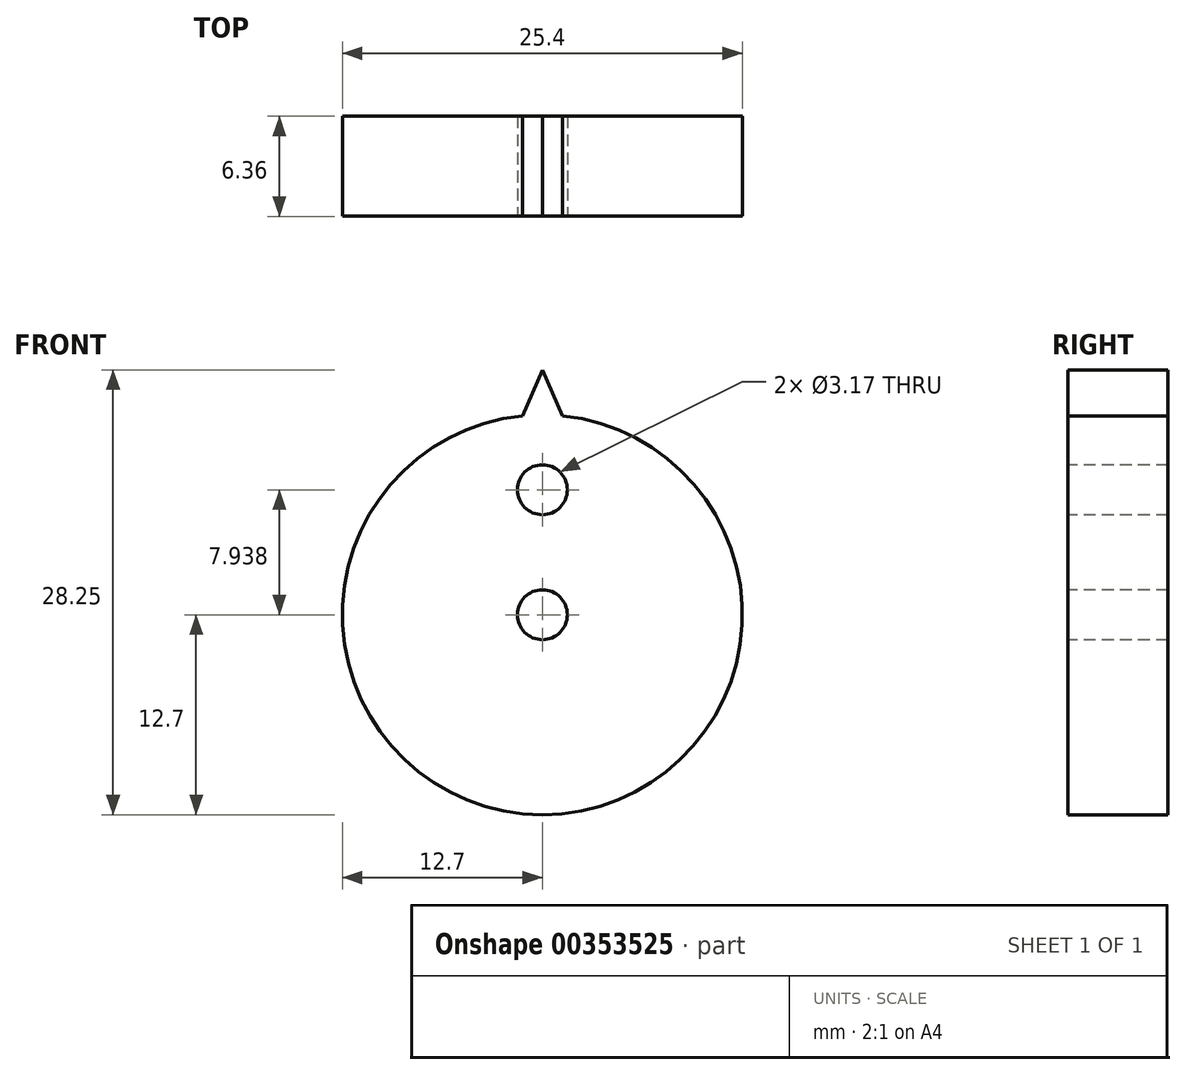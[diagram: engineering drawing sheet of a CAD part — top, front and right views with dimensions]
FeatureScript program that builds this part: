
annotation { "Feature Type Name" : "Feature", "Feature Type Description" : "" }
export const myFeature = defineFeature(function(context is Context, id is Id, definition is map)
    precondition{}
    {
        {
            var Q0;
            Q0=qCreatedBy(makeId("Front.planeOp"),FACE);
            var sketch = newSketch(context, id + "F0", { "sketchPlane" : qUnion([Q0])});
            skCircle(sketch, "E0", {"center": v(0, 0) * mm, "radius": 12.7 * mm});
            skSolve(sketch);
        }
        {
            var Q0;
            Q0 = qSketchRegion(id + "F0", true);
            var Q1;
            Q1 = qSketchRegion(id + "F2", true);
            extrude(context, id + "F1", {"entities" : qUnion([Q0, Q1]), "depth" : 6.35 * mm, "symmetric" : true});
        }
        {
            var Q0;
            Q0=makeQuery(id+"F1.opExtrude","CAP_FACE",FACE,{"disambiguationData":[OSD([sQuery(id+"F0.wireOp",EDGE,"E0")])],"isStart":false});
            var sketch = newSketch(context, id + "F2", { "sketchPlane" : qUnion([Q0])});
            skLineSegment(sketch, "E1", {"start": v(0, 0) * mm, "end": v(0, 12.7) * mm, "construction": true});
            skLineSegment(sketch, "E2", {"start": v(0, 12.7) * mm, "end": v(0, 0) * mm, "construction": true});
            skLineSegment(sketch, "E3", {"start": v(0, 0) * mm, "end": v(1.27, 12.64) * mm, "construction": true});
            skLineSegment(sketch, "E4", {"start": v(1.27, 12.64) * mm, "end": v(0, 12.7) * mm, "construction": true});
            skLineSegment(sketch, "E5", {"start": v(0, 0) * mm, "end": v(-1.27, 12.64) * mm, "construction": true});
            skLineSegment(sketch, "E6", {"start": v(-1.27, 12.64) * mm, "end": v(0, 12.7) * mm, "construction": true});
            skLineSegment(sketch, "E7", {"start": v(-1.27, 12.64) * mm, "end": v(0, 15.55) * mm, "construction": true});
            skLineSegment(sketch, "E8", {"start": v(0, 15.55) * mm, "end": v(1.27, 12.64) * mm, "construction": true});
            skLineSegment(sketch, "E9", {"start": v(-1.27, 12.64) * mm, "end": v(0, 15.55) * mm});
            skLineSegment(sketch, "E10", {"start": v(1.27, 12.64) * mm, "end": v(0, 15.55) * mm});
            skLineSegment(sketch, "E11", {"start": v(-1.27, 12.64) * mm, "end": v(1.27, 12.64) * mm});
            skSolve(sketch);
        }
        {
            var Q0;
            Q0 = qSketchRegion(id + "F2", true);
            extrude(context, id + "F3", {"entities" : qUnion([Q0]), "operationType" : NewBodyOperationType.ADD, "oppositeDirection" : true, "depth" : 6.35 * mm});
        }
        {
            var Q0;
            {var subQ0=sQuery(id+"F2.wireOp",EDGE,"E11");var subQ1=sQuery(id+"F2.wireOp",EDGE,"E10");var subQ2=sQuery(id+"F2.wireOp",EDGE,"E9");Q0=makeQuery(id+"FHqNzEV3IGper6F_1.29.F3.boolean.opBoolean","MERGE",FACE,{"derivedFrom":[makeQuery(id+"FHqNzEV3IGper6F_1.28.F3.boolean.opBoolean","MERGE",FACE,{"derivedFrom":[makeQuery(id+"FHqNzEV3IGper6F_1.27.F3.boolean.opBoolean","MERGE",FACE,{"derivedFrom":[makeQuery(id+"FHqNzEV3IGper6F_1.26.F3.boolean.opBoolean","MERGE",FACE,{"derivedFrom":[makeQuery(id+"FHqNzEV3IGper6F_1.25.F3.boolean.opBoolean","MERGE",FACE,{"derivedFrom":[makeQuery(id+"FHqNzEV3IGper6F_1.24.F3.boolean.opBoolean","MERGE",FACE,{"derivedFrom":[makeQuery(id+"FHqNzEV3IGper6F_1.23.F3.boolean.opBoolean","MERGE",FACE,{"derivedFrom":[makeQuery(id+"FHqNzEV3IGper6F_1.22.F3.boolean.opBoolean","MERGE",FACE,{"derivedFrom":[makeQuery(id+"FHqNzEV3IGper6F_1.21.F3.boolean.opBoolean","MERGE",FACE,{"derivedFrom":[makeQuery(id+"FHqNzEV3IGper6F_1.20.F3.boolean.opBoolean","MERGE",FACE,{"derivedFrom":[makeQuery(id+"FHqNzEV3IGper6F_1.19.F3.boolean.opBoolean","MERGE",FACE,{"derivedFrom":[makeQuery(id+"FHqNzEV3IGper6F_1.18.F3.boolean.opBoolean","MERGE",FACE,{"derivedFrom":[makeQuery(id+"FHqNzEV3IGper6F_1.17.F3.boolean.opBoolean","MERGE",FACE,{"derivedFrom":[makeQuery(id+"FHqNzEV3IGper6F_1.16.F3.boolean.opBoolean","MERGE",FACE,{"derivedFrom":[makeQuery(id+"FHqNzEV3IGper6F_1.15.F3.boolean.opBoolean","MERGE",FACE,{"derivedFrom":[makeQuery(id+"FHqNzEV3IGper6F_1.14.F3.boolean.opBoolean","MERGE",FACE,{"derivedFrom":[makeQuery(id+"FHqNzEV3IGper6F_1.13.F3.boolean.opBoolean","MERGE",FACE,{"derivedFrom":[makeQuery(id+"FHqNzEV3IGper6F_1.12.F3.boolean.opBoolean","MERGE",FACE,{"derivedFrom":[makeQuery(id+"FHqNzEV3IGper6F_1.11.F3.boolean.opBoolean","MERGE",FACE,{"derivedFrom":[makeQuery(id+"FHqNzEV3IGper6F_1.10.F3.boolean.opBoolean","MERGE",FACE,{"derivedFrom":[makeQuery(id+"FHqNzEV3IGper6F_1.9.F3.boolean.opBoolean","MERGE",FACE,{"derivedFrom":[makeQuery(id+"FHqNzEV3IGper6F_1.8.F3.boolean.opBoolean","MERGE",FACE,{"derivedFrom":[makeQuery(id+"FHqNzEV3IGper6F_1.7.F3.boolean.opBoolean","MERGE",FACE,{"derivedFrom":[makeQuery(id+"FHqNzEV3IGper6F_1.6.F3.boolean.opBoolean","MERGE",FACE,{"derivedFrom":[makeQuery(id+"FHqNzEV3IGper6F_1.5.F3.boolean.opBoolean","MERGE",FACE,{"derivedFrom":[makeQuery(id+"FHqNzEV3IGper6F_1.4.F3.boolean.opBoolean","MERGE",FACE,{"derivedFrom":[makeQuery(id+"FHqNzEV3IGper6F_1.3.F3.boolean.opBoolean","MERGE",FACE,{"derivedFrom":[makeQuery(id+"FHqNzEV3IGper6F_1.2.F3.boolean.opBoolean","MERGE",FACE,{"derivedFrom":[makeQuery(id+"FHqNzEV3IGper6F_1.1.F3.boolean.opBoolean","MERGE",FACE,{"derivedFrom":[makeQuery(id+"F3.boolean.opBoolean","MERGE",FACE,{"derivedFrom":[makeQuery(id+"F1.opExtrude","CAP_FACE",FACE,{"disambiguationData":[OSD([sQuery(id+"F0.wireOp",EDGE,"E0")])],"isStart":false}),makeQuery(id+"F3.opExtrude","CAP_FACE",FACE,{"disambiguationData":[OSD([subQ2,subQ1,subQ0])],"isStart":true})]}),makeQuery(id+"FHqNzEV3IGper6F_1.1.F3.opExtrude","CAP_FACE",FACE,{"disambiguationData":[OSD([subQ2,subQ1,subQ0])],"isStart":true})]}),makeQuery(id+"FHqNzEV3IGper6F_1.2.F3.opExtrude","CAP_FACE",FACE,{"disambiguationData":[OSD([subQ2,subQ1,subQ0])],"isStart":true})]}),makeQuery(id+"FHqNzEV3IGper6F_1.3.F3.opExtrude","CAP_FACE",FACE,{"disambiguationData":[OSD([subQ2,subQ1,subQ0])],"isStart":true})]}),makeQuery(id+"FHqNzEV3IGper6F_1.4.F3.opExtrude","CAP_FACE",FACE,{"disambiguationData":[OSD([subQ2,subQ1,subQ0])],"isStart":true})]}),makeQuery(id+"FHqNzEV3IGper6F_1.5.F3.opExtrude","CAP_FACE",FACE,{"disambiguationData":[OSD([subQ2,subQ1,subQ0])],"isStart":true})]}),makeQuery(id+"FHqNzEV3IGper6F_1.6.F3.opExtrude","CAP_FACE",FACE,{"disambiguationData":[OSD([subQ2,subQ1,subQ0])],"isStart":true})]}),makeQuery(id+"FHqNzEV3IGper6F_1.7.F3.opExtrude","CAP_FACE",FACE,{"disambiguationData":[OSD([subQ2,subQ1,subQ0])],"isStart":true})]}),makeQuery(id+"FHqNzEV3IGper6F_1.8.F3.opExtrude","CAP_FACE",FACE,{"disambiguationData":[OSD([subQ2,subQ1,subQ0])],"isStart":true})]}),makeQuery(id+"FHqNzEV3IGper6F_1.9.F3.opExtrude","CAP_FACE",FACE,{"disambiguationData":[OSD([subQ2,subQ1,subQ0])],"isStart":true})]}),makeQuery(id+"FHqNzEV3IGper6F_1.10.F3.opExtrude","CAP_FACE",FACE,{"disambiguationData":[OSD([subQ2,subQ1,subQ0])],"isStart":true})]}),makeQuery(id+"FHqNzEV3IGper6F_1.11.F3.opExtrude","CAP_FACE",FACE,{"disambiguationData":[OSD([subQ2,subQ1,subQ0])],"isStart":true})]}),makeQuery(id+"FHqNzEV3IGper6F_1.12.F3.opExtrude","CAP_FACE",FACE,{"disambiguationData":[OSD([subQ2,subQ1,subQ0])],"isStart":true})]}),makeQuery(id+"FHqNzEV3IGper6F_1.13.F3.opExtrude","CAP_FACE",FACE,{"disambiguationData":[OSD([subQ2,subQ1,subQ0])],"isStart":true})]}),makeQuery(id+"FHqNzEV3IGper6F_1.14.F3.opExtrude","CAP_FACE",FACE,{"disambiguationData":[OSD([subQ2,subQ1,subQ0])],"isStart":true})]}),makeQuery(id+"FHqNzEV3IGper6F_1.15.F3.opExtrude","CAP_FACE",FACE,{"disambiguationData":[OSD([subQ2,subQ1,subQ0])],"isStart":true})]}),makeQuery(id+"FHqNzEV3IGper6F_1.16.F3.opExtrude","CAP_FACE",FACE,{"disambiguationData":[OSD([subQ2,subQ1,subQ0])],"isStart":true})]}),makeQuery(id+"FHqNzEV3IGper6F_1.17.F3.opExtrude","CAP_FACE",FACE,{"disambiguationData":[OSD([subQ2,subQ1,subQ0])],"isStart":true})]}),makeQuery(id+"FHqNzEV3IGper6F_1.18.F3.opExtrude","CAP_FACE",FACE,{"disambiguationData":[OSD([subQ2,subQ1,subQ0])],"isStart":true})]}),makeQuery(id+"FHqNzEV3IGper6F_1.19.F3.opExtrude","CAP_FACE",FACE,{"disambiguationData":[OSD([subQ2,subQ1,subQ0])],"isStart":true})]}),makeQuery(id+"FHqNzEV3IGper6F_1.20.F3.opExtrude","CAP_FACE",FACE,{"disambiguationData":[OSD([subQ2,subQ1,subQ0])],"isStart":true})]}),makeQuery(id+"FHqNzEV3IGper6F_1.21.F3.opExtrude","CAP_FACE",FACE,{"disambiguationData":[OSD([subQ2,subQ1,subQ0])],"isStart":true})]}),makeQuery(id+"FHqNzEV3IGper6F_1.22.F3.opExtrude","CAP_FACE",FACE,{"disambiguationData":[OSD([subQ2,subQ1,subQ0])],"isStart":true})]}),makeQuery(id+"FHqNzEV3IGper6F_1.23.F3.opExtrude","CAP_FACE",FACE,{"disambiguationData":[OSD([subQ2,subQ1,subQ0])],"isStart":true})]}),makeQuery(id+"FHqNzEV3IGper6F_1.24.F3.opExtrude","CAP_FACE",FACE,{"disambiguationData":[OSD([subQ2,subQ1,subQ0])],"isStart":true})]}),makeQuery(id+"FHqNzEV3IGper6F_1.25.F3.opExtrude","CAP_FACE",FACE,{"disambiguationData":[OSD([subQ2,subQ1,subQ0])],"isStart":true})]}),makeQuery(id+"FHqNzEV3IGper6F_1.26.F3.opExtrude","CAP_FACE",FACE,{"disambiguationData":[OSD([subQ2,subQ1,subQ0])],"isStart":true})]}),makeQuery(id+"FHqNzEV3IGper6F_1.27.F3.opExtrude","CAP_FACE",FACE,{"disambiguationData":[OSD([subQ2,subQ1,subQ0])],"isStart":true})]}),makeQuery(id+"FHqNzEV3IGper6F_1.28.F3.opExtrude","CAP_FACE",FACE,{"disambiguationData":[OSD([subQ2,subQ1,subQ0])],"isStart":true})]}),makeQuery(id+"FHqNzEV3IGper6F_1.29.F3.opExtrude","CAP_FACE",FACE,{"disambiguationData":[OSD([subQ2,subQ1,subQ0])],"isStart":true})]});}
            var sketch = newSketch(context, id + "F4", { "sketchPlane" : qUnion([Q0])});
            skCircle(sketch, "E12", {"center": v(0, 0) * mm, "radius": 1.59 * mm});
            skSolve(sketch);
        }
        {
            var Q0;
            Q0 = qSketchRegion(id + "F4", true);
            extrude(context, id + "F5", {"entities" : qUnion([Q0]), "operationType" : NewBodyOperationType.REMOVE, "oppositeDirection" : true, "depth" : 6.35 * mm});
        }
        {
            var Q0;
            {var subQ0=sQuery(id+"F2.wireOp",EDGE,"E11");var subQ1=sQuery(id+"F2.wireOp",EDGE,"E10");var subQ2=sQuery(id+"F2.wireOp",EDGE,"E9");Q0=makeQuery(id+"FHqNzEV3IGper6F_1.29.F3.boolean.opBoolean","MERGE",FACE,{"derivedFrom":[makeQuery(id+"FHqNzEV3IGper6F_1.28.F3.boolean.opBoolean","MERGE",FACE,{"derivedFrom":[makeQuery(id+"FHqNzEV3IGper6F_1.27.F3.boolean.opBoolean","MERGE",FACE,{"derivedFrom":[makeQuery(id+"FHqNzEV3IGper6F_1.26.F3.boolean.opBoolean","MERGE",FACE,{"derivedFrom":[makeQuery(id+"FHqNzEV3IGper6F_1.25.F3.boolean.opBoolean","MERGE",FACE,{"derivedFrom":[makeQuery(id+"FHqNzEV3IGper6F_1.24.F3.boolean.opBoolean","MERGE",FACE,{"derivedFrom":[makeQuery(id+"FHqNzEV3IGper6F_1.23.F3.boolean.opBoolean","MERGE",FACE,{"derivedFrom":[makeQuery(id+"FHqNzEV3IGper6F_1.22.F3.boolean.opBoolean","MERGE",FACE,{"derivedFrom":[makeQuery(id+"FHqNzEV3IGper6F_1.21.F3.boolean.opBoolean","MERGE",FACE,{"derivedFrom":[makeQuery(id+"FHqNzEV3IGper6F_1.20.F3.boolean.opBoolean","MERGE",FACE,{"derivedFrom":[makeQuery(id+"FHqNzEV3IGper6F_1.19.F3.boolean.opBoolean","MERGE",FACE,{"derivedFrom":[makeQuery(id+"FHqNzEV3IGper6F_1.18.F3.boolean.opBoolean","MERGE",FACE,{"derivedFrom":[makeQuery(id+"FHqNzEV3IGper6F_1.17.F3.boolean.opBoolean","MERGE",FACE,{"derivedFrom":[makeQuery(id+"FHqNzEV3IGper6F_1.16.F3.boolean.opBoolean","MERGE",FACE,{"derivedFrom":[makeQuery(id+"FHqNzEV3IGper6F_1.15.F3.boolean.opBoolean","MERGE",FACE,{"derivedFrom":[makeQuery(id+"FHqNzEV3IGper6F_1.14.F3.boolean.opBoolean","MERGE",FACE,{"derivedFrom":[makeQuery(id+"FHqNzEV3IGper6F_1.13.F3.boolean.opBoolean","MERGE",FACE,{"derivedFrom":[makeQuery(id+"FHqNzEV3IGper6F_1.12.F3.boolean.opBoolean","MERGE",FACE,{"derivedFrom":[makeQuery(id+"FHqNzEV3IGper6F_1.11.F3.boolean.opBoolean","MERGE",FACE,{"derivedFrom":[makeQuery(id+"FHqNzEV3IGper6F_1.10.F3.boolean.opBoolean","MERGE",FACE,{"derivedFrom":[makeQuery(id+"FHqNzEV3IGper6F_1.9.F3.boolean.opBoolean","MERGE",FACE,{"derivedFrom":[makeQuery(id+"FHqNzEV3IGper6F_1.8.F3.boolean.opBoolean","MERGE",FACE,{"derivedFrom":[makeQuery(id+"FHqNzEV3IGper6F_1.7.F3.boolean.opBoolean","MERGE",FACE,{"derivedFrom":[makeQuery(id+"FHqNzEV3IGper6F_1.6.F3.boolean.opBoolean","MERGE",FACE,{"derivedFrom":[makeQuery(id+"FHqNzEV3IGper6F_1.5.F3.boolean.opBoolean","MERGE",FACE,{"derivedFrom":[makeQuery(id+"FHqNzEV3IGper6F_1.4.F3.boolean.opBoolean","MERGE",FACE,{"derivedFrom":[makeQuery(id+"FHqNzEV3IGper6F_1.3.F3.boolean.opBoolean","MERGE",FACE,{"derivedFrom":[makeQuery(id+"FHqNzEV3IGper6F_1.2.F3.boolean.opBoolean","MERGE",FACE,{"derivedFrom":[makeQuery(id+"FHqNzEV3IGper6F_1.1.F3.boolean.opBoolean","MERGE",FACE,{"derivedFrom":[makeQuery(id+"F3.boolean.opBoolean","MERGE",FACE,{"derivedFrom":[makeQuery(id+"F1.opExtrude","CAP_FACE",FACE,{"disambiguationData":[OSD([sQuery(id+"F0.wireOp",EDGE,"E0")])],"isStart":false}),makeQuery(id+"F3.opExtrude","CAP_FACE",FACE,{"disambiguationData":[OSD([subQ2,subQ1,subQ0])],"isStart":true})]}),makeQuery(id+"FHqNzEV3IGper6F_1.1.F3.opExtrude","CAP_FACE",FACE,{"disambiguationData":[OSD([subQ2,subQ1,subQ0])],"isStart":true})]}),makeQuery(id+"FHqNzEV3IGper6F_1.2.F3.opExtrude","CAP_FACE",FACE,{"disambiguationData":[OSD([subQ2,subQ1,subQ0])],"isStart":true})]}),makeQuery(id+"FHqNzEV3IGper6F_1.3.F3.opExtrude","CAP_FACE",FACE,{"disambiguationData":[OSD([subQ2,subQ1,subQ0])],"isStart":true})]}),makeQuery(id+"FHqNzEV3IGper6F_1.4.F3.opExtrude","CAP_FACE",FACE,{"disambiguationData":[OSD([subQ2,subQ1,subQ0])],"isStart":true})]}),makeQuery(id+"FHqNzEV3IGper6F_1.5.F3.opExtrude","CAP_FACE",FACE,{"disambiguationData":[OSD([subQ2,subQ1,subQ0])],"isStart":true})]}),makeQuery(id+"FHqNzEV3IGper6F_1.6.F3.opExtrude","CAP_FACE",FACE,{"disambiguationData":[OSD([subQ2,subQ1,subQ0])],"isStart":true})]}),makeQuery(id+"FHqNzEV3IGper6F_1.7.F3.opExtrude","CAP_FACE",FACE,{"disambiguationData":[OSD([subQ2,subQ1,subQ0])],"isStart":true})]}),makeQuery(id+"FHqNzEV3IGper6F_1.8.F3.opExtrude","CAP_FACE",FACE,{"disambiguationData":[OSD([subQ2,subQ1,subQ0])],"isStart":true})]}),makeQuery(id+"FHqNzEV3IGper6F_1.9.F3.opExtrude","CAP_FACE",FACE,{"disambiguationData":[OSD([subQ2,subQ1,subQ0])],"isStart":true})]}),makeQuery(id+"FHqNzEV3IGper6F_1.10.F3.opExtrude","CAP_FACE",FACE,{"disambiguationData":[OSD([subQ2,subQ1,subQ0])],"isStart":true})]}),makeQuery(id+"FHqNzEV3IGper6F_1.11.F3.opExtrude","CAP_FACE",FACE,{"disambiguationData":[OSD([subQ2,subQ1,subQ0])],"isStart":true})]}),makeQuery(id+"FHqNzEV3IGper6F_1.12.F3.opExtrude","CAP_FACE",FACE,{"disambiguationData":[OSD([subQ2,subQ1,subQ0])],"isStart":true})]}),makeQuery(id+"FHqNzEV3IGper6F_1.13.F3.opExtrude","CAP_FACE",FACE,{"disambiguationData":[OSD([subQ2,subQ1,subQ0])],"isStart":true})]}),makeQuery(id+"FHqNzEV3IGper6F_1.14.F3.opExtrude","CAP_FACE",FACE,{"disambiguationData":[OSD([subQ2,subQ1,subQ0])],"isStart":true})]}),makeQuery(id+"FHqNzEV3IGper6F_1.15.F3.opExtrude","CAP_FACE",FACE,{"disambiguationData":[OSD([subQ2,subQ1,subQ0])],"isStart":true})]}),makeQuery(id+"FHqNzEV3IGper6F_1.16.F3.opExtrude","CAP_FACE",FACE,{"disambiguationData":[OSD([subQ2,subQ1,subQ0])],"isStart":true})]}),makeQuery(id+"FHqNzEV3IGper6F_1.17.F3.opExtrude","CAP_FACE",FACE,{"disambiguationData":[OSD([subQ2,subQ1,subQ0])],"isStart":true})]}),makeQuery(id+"FHqNzEV3IGper6F_1.18.F3.opExtrude","CAP_FACE",FACE,{"disambiguationData":[OSD([subQ2,subQ1,subQ0])],"isStart":true})]}),makeQuery(id+"FHqNzEV3IGper6F_1.19.F3.opExtrude","CAP_FACE",FACE,{"disambiguationData":[OSD([subQ2,subQ1,subQ0])],"isStart":true})]}),makeQuery(id+"FHqNzEV3IGper6F_1.20.F3.opExtrude","CAP_FACE",FACE,{"disambiguationData":[OSD([subQ2,subQ1,subQ0])],"isStart":true})]}),makeQuery(id+"FHqNzEV3IGper6F_1.21.F3.opExtrude","CAP_FACE",FACE,{"disambiguationData":[OSD([subQ2,subQ1,subQ0])],"isStart":true})]}),makeQuery(id+"FHqNzEV3IGper6F_1.22.F3.opExtrude","CAP_FACE",FACE,{"disambiguationData":[OSD([subQ2,subQ1,subQ0])],"isStart":true})]}),makeQuery(id+"FHqNzEV3IGper6F_1.23.F3.opExtrude","CAP_FACE",FACE,{"disambiguationData":[OSD([subQ2,subQ1,subQ0])],"isStart":true})]}),makeQuery(id+"FHqNzEV3IGper6F_1.24.F3.opExtrude","CAP_FACE",FACE,{"disambiguationData":[OSD([subQ2,subQ1,subQ0])],"isStart":true})]}),makeQuery(id+"FHqNzEV3IGper6F_1.25.F3.opExtrude","CAP_FACE",FACE,{"disambiguationData":[OSD([subQ2,subQ1,subQ0])],"isStart":true})]}),makeQuery(id+"FHqNzEV3IGper6F_1.26.F3.opExtrude","CAP_FACE",FACE,{"disambiguationData":[OSD([subQ2,subQ1,subQ0])],"isStart":true})]}),makeQuery(id+"FHqNzEV3IGper6F_1.27.F3.opExtrude","CAP_FACE",FACE,{"disambiguationData":[OSD([subQ2,subQ1,subQ0])],"isStart":true})]}),makeQuery(id+"FHqNzEV3IGper6F_1.28.F3.opExtrude","CAP_FACE",FACE,{"disambiguationData":[OSD([subQ2,subQ1,subQ0])],"isStart":true})]}),makeQuery(id+"FHqNzEV3IGper6F_1.29.F3.opExtrude","CAP_FACE",FACE,{"disambiguationData":[OSD([subQ2,subQ1,subQ0])],"isStart":true})]});}
            var sketch = newSketch(context, id + "F6", { "sketchPlane" : qUnion([Q0])});
            skCircle(sketch, "E13", {"center": v(0, 7.94) * mm, "radius": 1.59 * mm});
            skSolve(sketch);
        }
        {
            var Q0;
            Q0 = qSketchRegion(id + "F6", true);
            extrude(context, id + "F7", {"entities" : qUnion([Q0]), "operationType" : NewBodyOperationType.REMOVE, "oppositeDirection" : true, "depth" : 6.35 * mm});
        }
    });
